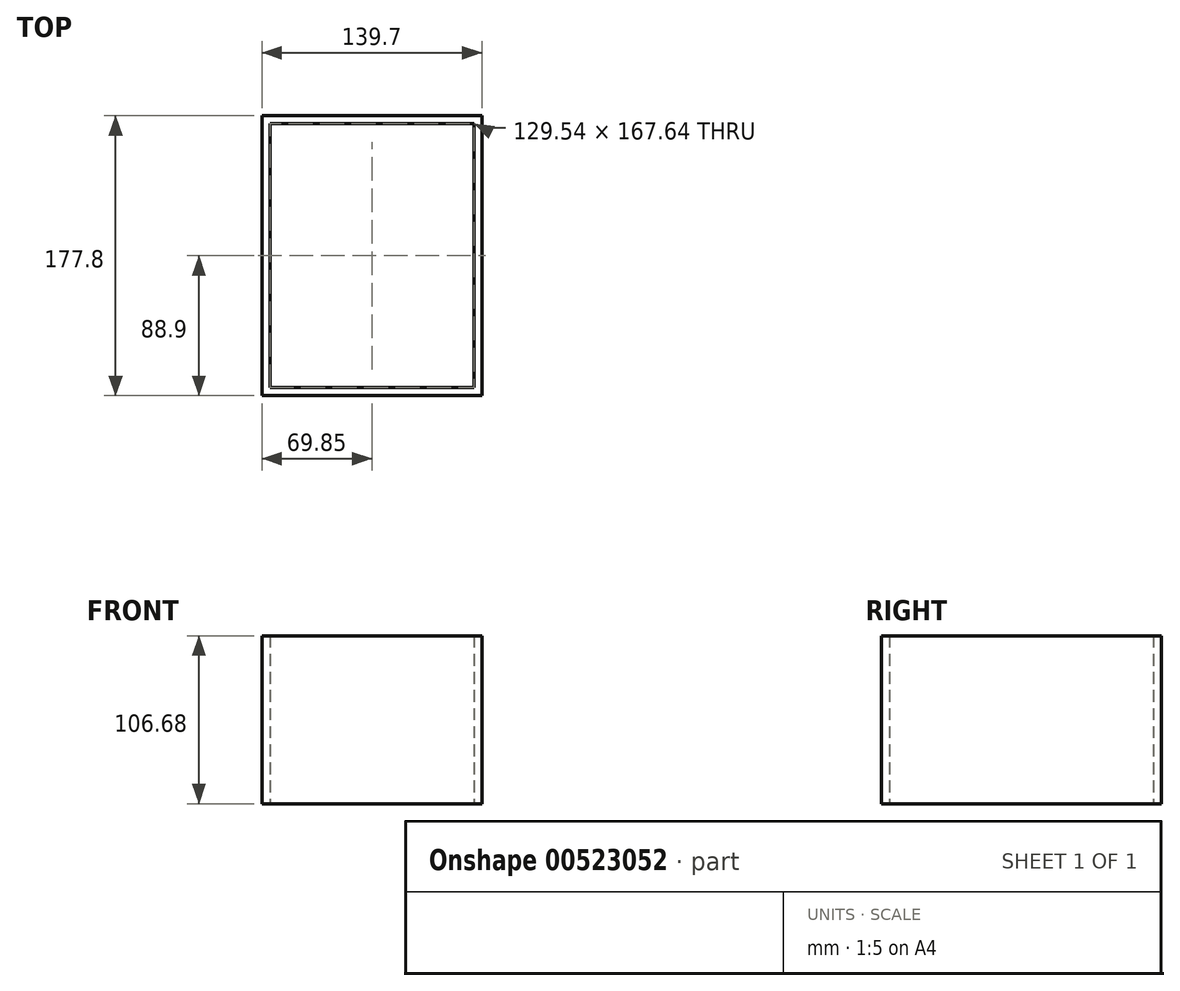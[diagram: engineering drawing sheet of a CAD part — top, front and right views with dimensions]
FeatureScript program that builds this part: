
annotation { "Feature Type Name" : "Feature", "Feature Type Description" : "" }
export const myFeature = defineFeature(function(context is Context, id is Id, definition is map)
    precondition{}
    {
        {
            var Q0;
            Q0=qCreatedBy(makeId("Top.planeOp"),FACE);
            var sketch = newSketch(context, id + "F0", { "sketchPlane" : qUnion([Q0])});
            skLineSegment(sketch, "E0.bottom", {"start": v(0, 0) * mm, "end": v(139.7, 0) * mm});
            skLineSegment(sketch, "E0.top", {"start": v(0, -177.8) * mm, "end": v(139.7, -177.8) * mm});
            skLineSegment(sketch, "E0.left", {"start": v(0, 0) * mm, "end": v(0, -177.8) * mm});
            skLineSegment(sketch, "E0.right", {"start": v(139.7, 0) * mm, "end": v(139.7, -177.8) * mm});
            skLineSegment(sketch, "E1.bottom", {"start": v(5.08, -5.08) * mm, "end": v(134.62, -5.08) * mm});
            skLineSegment(sketch, "E1.top", {"start": v(5.08, -172.72) * mm, "end": v(134.62, -172.72) * mm});
            skLineSegment(sketch, "E1.left", {"start": v(5.08, -5.08) * mm, "end": v(5.08, -172.72) * mm});
            skLineSegment(sketch, "E1.right", {"start": v(134.62, -5.08) * mm, "end": v(134.62, -172.72) * mm});
            skSolve(sketch);
        }
        {
            var Q0;
            Q0 = qSketchRegion(id + "F0", true);
            extrude(context, id + "F1", {"entities" : qUnion([Q0]), "depth" : 106.68 * mm, "offsetDistance" : 25.4 * mm});
        }
    });
